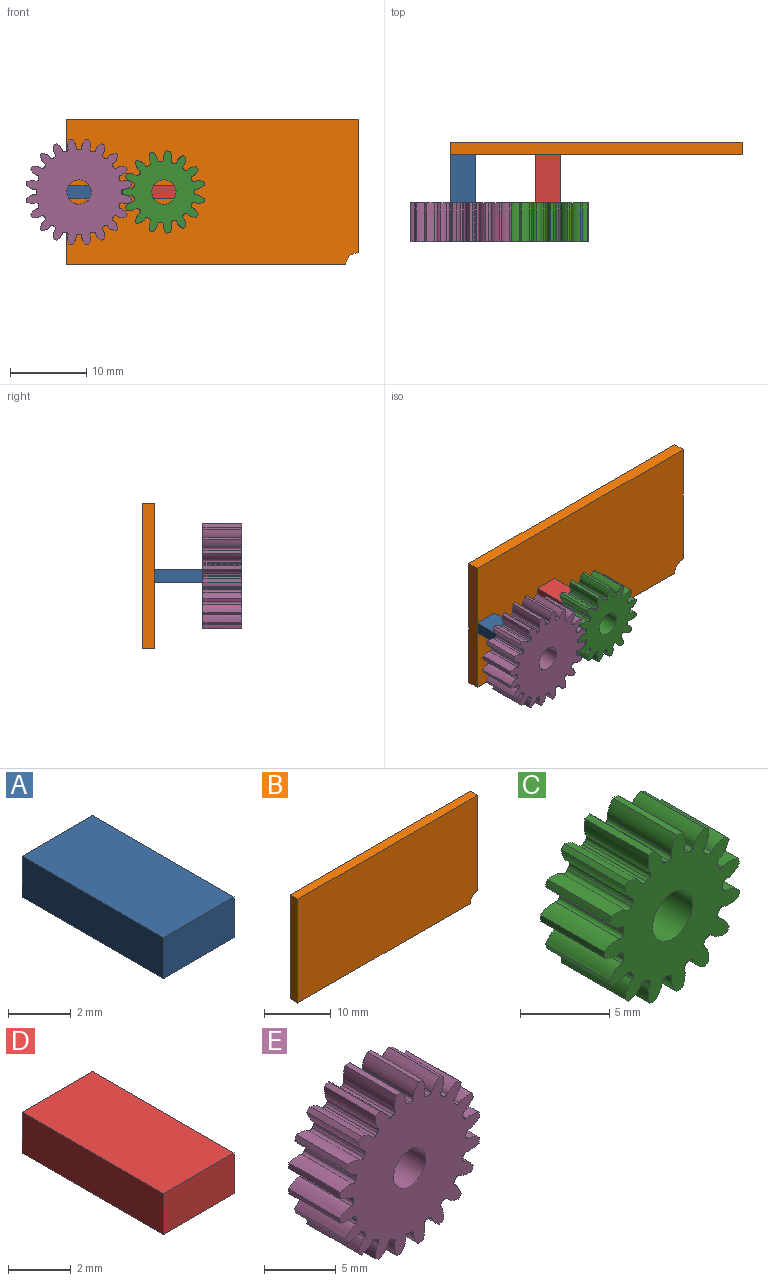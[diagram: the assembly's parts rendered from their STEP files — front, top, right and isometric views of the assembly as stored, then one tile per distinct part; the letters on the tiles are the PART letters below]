
ASSEMBLY  parts=5 mates=3
PART A: 6 faces, bbox 3.2x6.4x1.6 mm
  f0: plane 6.35x1.59mm, normal (-1,0,0), area 10.1mm2, adj f1,f3,f4,f5
  f1: plane 6.35x3.18mm, normal (0,0,-1), area 20.2mm2, adj f0,f2,f4,f5
  f2: plane 6.35x1.59mm, normal (1,0,0), area 10.1mm2, adj f1,f3,f4,f5
  f3: plane 6.35x3.18mm, normal (0,0,1), area 20.2mm2, adj f0,f2,f4,f5
  f4: plane 3.18x1.59mm, normal (0,-1,0), area 5mm2, adj f0,f1,f2,f3
  f5: plane 3.18x1.59mm, normal (0,1,0), area 5mm2, adj f0,f1,f2,f3
PART B: 7 faces, bbox 38.1x1.6x19.1 mm
  f0: plane 19.05x1.59mm, normal (-1,0,0), area 30.2mm2, adj f1,f3,f4,f5
  f1: plane 36.51x1.59mm, normal (0,0,-1), area 58mm2, adj f0,f4,f5,f6
  f2: plane 17.46x1.59mm, normal (1,0,0), area 27.7mm2, adj f3,f4,f5,f6
  f3: plane 38.1x1.59mm, normal (0,0,1), area 60.5mm2, adj f0,f2,f4,f5
  f4: plane 38.1x19.05mm, normal (0,-1,0), area 723.8mm2, adj f0,f1,f2,f3,f6
  f5: plane 38.1x19.05mm, normal (0,1,0), area 723.8mm2, adj f0,f1,f2,f3,f6
  f6: cylinder r=1.59mm len=1.59mm, axis (0,-1,0), area 4mm2, adj f1,f2,f4,f5
PART C: 93 faces, bbox 10.7x5.1x10.8 mm
  f0: cylinder r=5.4mm len=5.08mm, axis (0,1,0), area 2.1mm2, adj f14,f16,f82,f89
  f1: cylinder r=5.4mm len=5.08mm, axis (0,1,0), area 2.1mm2, adj f14,f16,f72,f84
  f2: cylinder r=5.4mm len=5.08mm, axis (0,1,0), area 2.1mm2, adj f14,f16,f17,f79
  f3: cylinder r=5.4mm len=5.08mm, axis (0,1,0), area 2.1mm2, adj f14,f16,f74,f77
  f4: cylinder r=5.4mm len=5.08mm, axis (0,1,0), area 2.1mm2, adj f14,f16,f62,f69
  f5: cylinder r=5.4mm len=5.08mm, axis (0,1,0), area 2.1mm2, adj f14,f16,f64,f87
  f6: cylinder r=5.4mm len=5.08mm, axis (0,1,0), area 2.1mm2, adj f14,f16,f59,f67
  f7: cylinder r=5.4mm len=5.08mm, axis (0,1,0), area 2.1mm2, adj f14,f16,f54,f57
  f8: cylinder r=5.4mm len=5.08mm, axis (0,1,0), area 2.1mm2, adj f14,f16,f37,f49
  f9: cylinder r=5.4mm len=5.08mm, axis (0,1,0), area 2.1mm2, adj f14,f16,f44,f47
  f10: cylinder r=5.4mm len=5.08mm, axis (0,1,0), area 2.1mm2, adj f14,f16,f32,f39
  f11: cylinder r=5.4mm len=5.08mm, axis (0,1,0), area 2.1mm2, adj f14,f16,f22,f34
  f12: cylinder r=5.4mm len=5.08mm, axis (0,1,0), area 2.1mm2, adj f14,f16,f29,f52
  f13: cylinder r=5.4mm len=5.08mm, axis (0,1,0), area 2.1mm2, adj f14,f16,f24,f27
  f14: plane 10.79x10.73mm, normal (0,-1,0), area 61.3mm2, adj f0,f1,f2,f3,f4,f5,f6,f7
  f15: cylinder r=5.4mm len=5.08mm, axis (0,1,0), area 2.1mm2, adj f14,f16,f19,f42
  f16: plane 10.79x10.73mm, normal (0,1,0), area 61.3mm2, adj f0,f1,f2,f3,f4,f5,f6,f7
  f17: extruded ~5.08x1.11mm, area 6.5mm2, adj f2,f14,f16,f20
  f18: cylinder r=3.97mm len=5.08mm, axis (0,1,0), area 1.1mm2, adj f14,f16,f20,f21
  f19: extruded ~5.08x1.11mm, area 6.5mm2, adj f14,f15,f16,f21
  f20: cylinder r=0.26mm len=5.08mm, axis (0,1,0), area 2mm2, adj f14,f16,f17,f18
  f21: cylinder r=0.26mm len=5.08mm, axis (0,1,0), area 2mm2, adj f14,f16,f18,f19
  f22: extruded ~5.08x1.24mm, area 6.5mm2, adj f11,f14,f16,f25
  f23: cylinder r=3.97mm len=5.08mm, axis (0,1,0), area 1.1mm2, adj f14,f16,f25,f26
  f24: extruded ~5.08x1.03mm, area 6.5mm2, adj f13,f14,f16,f26
  f25: cylinder r=0.26mm len=5.08mm, axis (0,1,0), area 2mm2, adj f14,f16,f22,f23
  f26: cylinder r=0.26mm len=5.08mm, axis (0,1,0), area 2mm2, adj f14,f16,f23,f24
  f27: extruded ~5.08x1.09mm, area 6.5mm2, adj f13,f14,f16,f30
  f28: cylinder r=3.97mm len=5.08mm, axis (0,1,0), area 1.1mm2, adj f14,f16,f30,f31
  f29: extruded ~5.08x1.22mm, area 6.5mm2, adj f12,f14,f16,f31
  f30: cylinder r=0.26mm len=5.08mm, axis (0,1,0), area 2mm2, adj f14,f16,f27,f28
  f31: cylinder r=0.26mm len=5.08mm, axis (0,1,0), area 2mm2, adj f14,f16,f28,f29
  f32: extruded ~5.08x1.17mm, area 6.5mm2, adj f10,f14,f16,f35
  f33: cylinder r=3.97mm len=5.08mm, axis (0,1,0), area 1.1mm2, adj f14,f16,f35,f36
  f34: extruded ~5.08x1.05mm, area 6.5mm2, adj f11,f14,f16,f36
  f35: cylinder r=0.26mm len=5.08mm, axis (0,1,0), area 2mm2, adj f14,f16,f32,f33
  f36: cylinder r=0.26mm len=5.08mm, axis (0,1,0), area 2mm2, adj f14,f16,f33,f34
  f37: extruded ~5.08x0.89mm, area 6.5mm2, adj f8,f14,f16,f40
  f38: cylinder r=3.97mm len=5.08mm, axis (0,1,0), area 1.1mm2, adj f14,f16,f40,f41
  f39: extruded ~5.08x1.23mm, area 6.5mm2, adj f10,f14,f16,f41
  f40: cylinder r=0.26mm len=5.08mm, axis (0,1,0), area 2mm2, adj f14,f16,f37,f38
  f41: cylinder r=0.26mm len=5.08mm, axis (0,1,0), area 2mm2, adj f14,f16,f38,f39
  f42: extruded ~5.08x1.24mm, area 6.5mm2, adj f14,f15,f16,f45
  f43: cylinder r=3.97mm len=5.08mm, axis (0,1,0), area 1.1mm2, adj f14,f16,f45,f46
  f44: extruded ~5.08x0.95mm, area 6.5mm2, adj f9,f14,f16,f46
  f45: cylinder r=0.26mm len=5.08mm, axis (0,1,0), area 2mm2, adj f14,f16,f42,f43
  f46: cylinder r=0.26mm len=5.08mm, axis (0,1,0), area 2mm2, adj f14,f16,f43,f44
  f47: extruded ~5.08x1.15mm, area 6.5mm2, adj f9,f14,f16,f50
  f48: cylinder r=3.97mm len=5.08mm, axis (0,1,0), area 1.1mm2, adj f14,f16,f50,f51
  f49: extruded ~5.08x1.19mm, area 6.5mm2, adj f8,f14,f16,f51
  f50: cylinder r=0.26mm len=5.08mm, axis (0,1,0), area 2mm2, adj f14,f16,f47,f48
  f51: cylinder r=0.26mm len=5.08mm, axis (0,1,0), area 2mm2, adj f14,f16,f48,f49
  f52: extruded ~5.08x0.98mm, area 6.5mm2, adj f12,f14,f16,f55
  f53: cylinder r=3.97mm len=5.08mm, axis (0,1,0), area 1.1mm2, adj f14,f16,f55,f56
  f54: extruded ~5.08x1.2mm, area 6.5mm2, adj f7,f14,f16,f56
  f55: cylinder r=0.26mm len=5.08mm, axis (0,1,0), area 2mm2, adj f14,f16,f52,f53
  f56: cylinder r=0.26mm len=5.08mm, axis (0,1,0), area 2mm2, adj f14,f16,f53,f54
  f57: extruded ~5.08x1.2mm, area 6.5mm2, adj f7,f14,f16,f60
  f58: cylinder r=3.97mm len=5.08mm, axis (0,1,0), area 1.1mm2, adj f14,f16,f60,f61
  f59: extruded ~5.08x0.98mm, area 6.5mm2, adj f6,f14,f16,f61
  f60: cylinder r=0.26mm len=5.08mm, axis (0,1,0), area 2mm2, adj f14,f16,f57,f58
  f61: cylinder r=0.26mm len=5.08mm, axis (0,1,0), area 2mm2, adj f14,f16,f58,f59
  f62: extruded ~5.08x1.03mm, area 6.5mm2, adj f4,f14,f16,f65
  f63: cylinder r=3.97mm len=5.08mm, axis (0,1,0), area 1.1mm2, adj f14,f16,f65,f66
  f64: extruded ~5.08x1.24mm, area 6.5mm2, adj f5,f14,f16,f66
  f65: cylinder r=0.26mm len=5.08mm, axis (0,1,0), area 2mm2, adj f14,f16,f62,f63
  f66: cylinder r=0.26mm len=5.08mm, axis (0,1,0), area 2mm2, adj f14,f16,f63,f64
  f67: extruded ~5.08x1.22mm, area 6.5mm2, adj f6,f14,f16,f70
  f68: cylinder r=3.97mm len=5.08mm, axis (0,1,0), area 1.1mm2, adj f14,f16,f70,f71
  f69: extruded ~5.08x1.09mm, area 6.5mm2, adj f4,f14,f16,f71
  f70: cylinder r=0.26mm len=5.08mm, axis (0,1,0), area 2mm2, adj f14,f16,f67,f68
  f71: cylinder r=0.26mm len=5.08mm, axis (0,1,0), area 2mm2, adj f14,f16,f68,f69
  f72: extruded ~5.08x1.19mm, area 6.5mm2, adj f1,f14,f16,f75
  f73: cylinder r=3.97mm len=5.08mm, axis (0,1,0), area 1.1mm2, adj f14,f16,f75,f76
  f74: extruded ~5.08x1.15mm, area 6.5mm2, adj f3,f14,f16,f76
  f75: cylinder r=0.26mm len=5.08mm, axis (0,1,0), area 2mm2, adj f14,f16,f72,f73
  f76: cylinder r=0.26mm len=5.08mm, axis (0,1,0), area 2mm2, adj f14,f16,f73,f74
  f77: extruded ~5.08x0.95mm, area 6.5mm2, adj f3,f14,f16,f80
  f78: cylinder r=3.97mm len=5.08mm, axis (0,1,0), area 1.1mm2, adj f14,f16,f80,f81
  f79: extruded ~5.08x1.24mm, area 6.5mm2, adj f2,f14,f16,f81
  f80: cylinder r=0.26mm len=5.08mm, axis (0,1,0), area 2mm2, adj f14,f16,f77,f78
  f81: cylinder r=0.26mm len=5.08mm, axis (0,1,0), area 2mm2, adj f14,f16,f78,f79
  f82: extruded ~5.08x1.23mm, area 6.5mm2, adj f0,f14,f16,f85
  f83: cylinder r=3.97mm len=5.08mm, axis (0,1,0), area 1.1mm2, adj f14,f16,f85,f86
  f84: extruded ~5.08x0.89mm, area 6.5mm2, adj f1,f14,f16,f86
  f85: cylinder r=0.26mm len=5.08mm, axis (0,1,0), area 2mm2, adj f14,f16,f82,f83
  f86: cylinder r=0.26mm len=5.08mm, axis (0,1,0), area 2mm2, adj f14,f16,f83,f84
  f87: extruded ~5.08x1.05mm, area 6.5mm2, adj f5,f14,f16,f90
  f88: cylinder r=3.97mm len=5.08mm, axis (0,1,0), area 1.1mm2, adj f14,f16,f90,f91
  f89: extruded ~5.08x1.17mm, area 6.5mm2, adj f0,f14,f16,f91
  f90: cylinder r=0.26mm len=5.08mm, axis (0,1,0), area 2mm2, adj f14,f16,f87,f88
  f91: cylinder r=0.26mm len=5.08mm, axis (0,1,0), area 2mm2, adj f14,f16,f88,f89
  f92: cylinder r=1.59mm len=5.08mm, axis (0,-1,0), area 50.7mm2, adj f14,f16
PART D: 6 faces, bbox 3.2x6.4x1.6 mm
  f0: plane 6.35x1.59mm, normal (-1,0,0), area 10.1mm2, adj f1,f3,f4,f5
  f1: plane 6.35x3.18mm, normal (0,0,-1), area 20.2mm2, adj f0,f2,f4,f5
  f2: plane 6.35x1.59mm, normal (1,0,0), area 10.1mm2, adj f1,f3,f4,f5
  f3: plane 6.35x3.18mm, normal (0,0,1), area 20.2mm2, adj f0,f2,f4,f5
  f4: plane 3.18x1.59mm, normal (0,-1,0), area 5mm2, adj f0,f1,f2,f3
  f5: plane 3.18x1.59mm, normal (0,1,0), area 5mm2, adj f0,f1,f2,f3
PART E: 123 faces, bbox 13.9x5.1x13.9 mm
  f0: cylinder r=6.99mm len=5.08mm, axis (0,1,0), area 2.2mm2, adj f19,f21,f72,f119
  f1: cylinder r=6.99mm len=5.08mm, axis (0,1,0), area 2.2mm2, adj f19,f21,f114,f117
  f2: cylinder r=6.99mm len=5.08mm, axis (0,1,0), area 2.2mm2, adj f19,f21,f109,f112
  f3: cylinder r=6.99mm len=5.08mm, axis (0,1,0), area 2.2mm2, adj f19,f21,f104,f107
  f4: cylinder r=6.99mm len=5.08mm, axis (0,1,0), area 2.2mm2, adj f19,f21,f99,f102
  f5: cylinder r=6.99mm len=5.08mm, axis (0,1,0), area 2.2mm2, adj f19,f21,f94,f97
  f6: cylinder r=6.99mm len=5.08mm, axis (0,1,0), area 2.2mm2, adj f19,f21,f89,f92
  f7: cylinder r=6.99mm len=5.08mm, axis (0,1,0), area 2.2mm2, adj f19,f21,f84,f87
  f8: cylinder r=6.99mm len=5.08mm, axis (0,1,0), area 2.2mm2, adj f19,f21,f67,f79
  f9: cylinder r=6.99mm len=5.08mm, axis (0,1,0), area 2.2mm2, adj f19,f21,f74,f77
  f10: cylinder r=6.99mm len=5.08mm, axis (0,1,0), area 2.2mm2, adj f19,f21,f62,f69
  f11: cylinder r=6.99mm len=5.08mm, axis (0,1,0), area 2.2mm2, adj f19,f21,f42,f64
  f12: cylinder r=6.99mm len=5.08mm, axis (0,1,0), area 2.2mm2, adj f19,f21,f22,f59
  f13: cylinder r=6.99mm len=5.08mm, axis (0,1,0), area 2.2mm2, adj f19,f21,f54,f57
  f14: cylinder r=6.99mm len=5.08mm, axis (0,1,0), area 2.2mm2, adj f19,f21,f49,f52
  f15: cylinder r=6.99mm len=5.08mm, axis (0,1,0), area 2.2mm2, adj f19,f21,f44,f47
  f16: cylinder r=6.99mm len=5.08mm, axis (0,1,0), area 2.2mm2, adj f19,f21,f32,f39
  f17: cylinder r=6.99mm len=5.08mm, axis (0,1,0), area 2.2mm2, adj f19,f21,f34,f82
  f18: cylinder r=6.99mm len=5.08mm, axis (0,1,0), area 2.2mm2, adj f19,f21,f29,f37
  f19: plane 13.87x13.87mm, normal (0,-1,0), area 116.2mm2, adj f0,f1,f2,f3,f4,f5,f6,f7
  f20: cylinder r=6.99mm len=5.08mm, axis (0,1,0), area 2.2mm2, adj f19,f21,f24,f27
  f21: plane 13.87x13.87mm, normal (0,1,0), area 116.2mm2, adj f0,f1,f2,f3,f4,f5,f6,f7
  f22: extruded ~5.08x1.14mm, area 6.5mm2, adj f12,f19,f21,f25
  f23: cylinder r=5.56mm len=5.08mm, axis (0,1,0), area 1.1mm2, adj f19,f21,f25,f26
  f24: extruded ~5.08x1.14mm, area 6.5mm2, adj f19,f20,f21,f26
  f25: cylinder r=0.25mm len=5.08mm, axis (0,1,0), area 2mm2, adj f19,f21,f22,f23
  f26: cylinder r=0.25mm len=5.08mm, axis (0,1,0), area 2mm2, adj f19,f21,f23,f24
  f27: extruded ~5.08x1.24mm, area 6.5mm2, adj f19,f20,f21,f30
  f28: cylinder r=5.56mm len=5.08mm, axis (0,1,0), area 1.1mm2, adj f19,f21,f30,f31
  f29: extruded ~5.08x0.93mm, area 6.5mm2, adj f18,f19,f21,f31
  f30: cylinder r=0.25mm len=5.08mm, axis (0,1,0), area 2mm2, adj f19,f21,f27,f28
  f31: cylinder r=0.25mm len=5.08mm, axis (0,1,0), area 2mm2, adj f19,f21,f28,f29
  f32: extruded ~5.08x1.08mm, area 6.5mm2, adj f16,f19,f21,f35
  f33: cylinder r=5.56mm len=5.08mm, axis (0,1,0), area 1.1mm2, adj f19,f21,f35,f36
  f34: extruded ~5.08x1.22mm, area 6.5mm2, adj f17,f19,f21,f36
  f35: cylinder r=0.25mm len=5.08mm, axis (0,1,0), area 2mm2, adj f19,f21,f32,f33
  f36: cylinder r=0.25mm len=5.08mm, axis (0,1,0), area 2mm2, adj f19,f21,f33,f34
  f37: extruded ~5.08x1.22mm, area 6.5mm2, adj f18,f19,f21,f40
  f38: cylinder r=5.56mm len=5.08mm, axis (0,1,0), area 1.1mm2, adj f19,f21,f40,f41
  f39: extruded ~5.08x1.08mm, area 6.5mm2, adj f16,f19,f21,f41
  f40: cylinder r=0.25mm len=5.08mm, axis (0,1,0), area 2mm2, adj f19,f21,f37,f38
  f41: cylinder r=0.25mm len=5.08mm, axis (0,1,0), area 2mm2, adj f19,f21,f38,f39
  f42: extruded ~5.08x1.24mm, area 6.5mm2, adj f11,f19,f21,f45
  f43: cylinder r=5.56mm len=5.08mm, axis (0,1,0), area 1.1mm2, adj f19,f21,f45,f46
  f44: extruded ~5.08x0.93mm, area 6.5mm2, adj f15,f19,f21,f46
  f45: cylinder r=0.25mm len=5.08mm, axis (0,1,0), area 2mm2, adj f19,f21,f42,f43
  f46: cylinder r=0.25mm len=5.08mm, axis (0,1,0), area 2mm2, adj f19,f21,f43,f44
  f47: extruded ~5.08x1.22mm, area 6.5mm2, adj f15,f19,f21,f50
  f48: cylinder r=5.56mm len=5.08mm, axis (0,1,0), area 1.1mm2, adj f19,f21,f50,f51
  f49: extruded ~5.08x1.08mm, area 6.5mm2, adj f14,f19,f21,f51
  f50: cylinder r=0.25mm len=5.08mm, axis (0,1,0), area 2mm2, adj f19,f21,f47,f48
  f51: cylinder r=0.25mm len=5.08mm, axis (0,1,0), area 2mm2, adj f19,f21,f48,f49
  f52: extruded ~5.08x1.08mm, area 6.5mm2, adj f14,f19,f21,f55
  f53: cylinder r=5.56mm len=5.08mm, axis (0,1,0), area 1.1mm2, adj f19,f21,f55,f56
  f54: extruded ~5.08x1.22mm, area 6.5mm2, adj f13,f19,f21,f56
  f55: cylinder r=0.25mm len=5.08mm, axis (0,1,0), area 2mm2, adj f19,f21,f52,f53
  f56: cylinder r=0.25mm len=5.08mm, axis (0,1,0), area 2mm2, adj f19,f21,f53,f54
  f57: extruded ~5.08x0.93mm, area 6.5mm2, adj f13,f19,f21,f60
  f58: cylinder r=5.56mm len=5.08mm, axis (0,1,0), area 1.1mm2, adj f19,f21,f60,f61
  f59: extruded ~5.08x1.24mm, area 6.5mm2, adj f12,f19,f21,f61
  f60: cylinder r=0.25mm len=5.08mm, axis (0,1,0), area 2mm2, adj f19,f21,f57,f58
  f61: cylinder r=0.25mm len=5.08mm, axis (0,1,0), area 2mm2, adj f19,f21,f58,f59
  f62: extruded ~5.08x1.14mm, area 6.5mm2, adj f10,f19,f21,f65
  f63: cylinder r=5.56mm len=5.08mm, axis (0,1,0), area 1.1mm2, adj f19,f21,f65,f66
  f64: extruded ~5.08x1.14mm, area 6.5mm2, adj f11,f19,f21,f66
  f65: cylinder r=0.25mm len=5.08mm, axis (0,1,0), area 2mm2, adj f19,f21,f62,f63
  f66: cylinder r=0.25mm len=5.08mm, axis (0,1,0), area 2mm2, adj f19,f21,f63,f64
  f67: extruded ~5.08x0.93mm, area 6.5mm2, adj f8,f19,f21,f70
  f68: cylinder r=5.56mm len=5.08mm, axis (0,1,0), area 1.1mm2, adj f19,f21,f70,f71
  f69: extruded ~5.08x1.24mm, area 6.5mm2, adj f10,f19,f21,f71
  f70: cylinder r=0.25mm len=5.08mm, axis (0,1,0), area 2mm2, adj f19,f21,f67,f68
  f71: cylinder r=0.25mm len=5.08mm, axis (0,1,0), area 2mm2, adj f19,f21,f68,f69
  f72: extruded ~5.08x1.22mm, area 6.5mm2, adj f0,f19,f21,f75
  f73: cylinder r=5.56mm len=5.08mm, axis (0,1,0), area 1.1mm2, adj f19,f21,f75,f76
  f74: extruded ~5.08x1.08mm, area 6.5mm2, adj f9,f19,f21,f76
  f75: cylinder r=0.25mm len=5.08mm, axis (0,1,0), area 2mm2, adj f19,f21,f72,f73
  f76: cylinder r=0.25mm len=5.08mm, axis (0,1,0), area 2mm2, adj f19,f21,f73,f74
  f77: extruded ~5.08x1.08mm, area 6.5mm2, adj f9,f19,f21,f80
  f78: cylinder r=5.56mm len=5.08mm, axis (0,1,0), area 1.1mm2, adj f19,f21,f80,f81
  f79: extruded ~5.08x1.22mm, area 6.5mm2, adj f8,f19,f21,f81
  f80: cylinder r=0.25mm len=5.08mm, axis (0,1,0), area 2mm2, adj f19,f21,f77,f78
  f81: cylinder r=0.25mm len=5.08mm, axis (0,1,0), area 2mm2, adj f19,f21,f78,f79
  f82: extruded ~5.08x0.93mm, area 6.5mm2, adj f17,f19,f21,f85
  f83: cylinder r=5.56mm len=5.08mm, axis (0,1,0), area 1.1mm2, adj f19,f21,f85,f86
  f84: extruded ~5.08x1.24mm, area 6.5mm2, adj f7,f19,f21,f86
  f85: cylinder r=0.25mm len=5.08mm, axis (0,1,0), area 2mm2, adj f19,f21,f82,f83
  f86: cylinder r=0.25mm len=5.08mm, axis (0,1,0), area 2mm2, adj f19,f21,f83,f84
  f87: extruded ~5.08x1.14mm, area 6.5mm2, adj f7,f19,f21,f90
  f88: cylinder r=5.56mm len=5.08mm, axis (0,1,0), area 1.1mm2, adj f19,f21,f90,f91
  f89: extruded ~5.08x1.14mm, area 6.5mm2, adj f6,f19,f21,f91
  f90: cylinder r=0.25mm len=5.08mm, axis (0,1,0), area 2mm2, adj f19,f21,f87,f88
  f91: cylinder r=0.25mm len=5.08mm, axis (0,1,0), area 2mm2, adj f19,f21,f88,f89
  f92: extruded ~5.08x1.24mm, area 6.5mm2, adj f6,f19,f21,f95
  f93: cylinder r=5.56mm len=5.08mm, axis (0,1,0), area 1.1mm2, adj f19,f21,f95,f96
  f94: extruded ~5.08x0.93mm, area 6.5mm2, adj f5,f19,f21,f96
  f95: cylinder r=0.25mm len=5.08mm, axis (0,1,0), area 2mm2, adj f19,f21,f92,f93
  f96: cylinder r=0.25mm len=5.08mm, axis (0,1,0), area 2mm2, adj f19,f21,f93,f94
  f97: extruded ~5.08x1.22mm, area 6.5mm2, adj f5,f19,f21,f100
  f98: cylinder r=5.56mm len=5.08mm, axis (0,1,0), area 1.1mm2, adj f19,f21,f100,f101
  f99: extruded ~5.08x1.08mm, area 6.5mm2, adj f4,f19,f21,f101
  f100: cylinder r=0.25mm len=5.08mm, axis (0,1,0), area 2mm2, adj f19,f21,f97,f98
  f101: cylinder r=0.25mm len=5.08mm, axis (0,1,0), area 2mm2, adj f19,f21,f98,f99
  f102: extruded ~5.08x1.08mm, area 6.5mm2, adj f4,f19,f21,f105
  f103: cylinder r=5.56mm len=5.08mm, axis (0,1,0), area 1.1mm2, adj f19,f21,f105,f106
  f104: extruded ~5.08x1.22mm, area 6.5mm2, adj f3,f19,f21,f106
  f105: cylinder r=0.25mm len=5.08mm, axis (0,1,0), area 2mm2, adj f19,f21,f102,f103
  f106: cylinder r=0.25mm len=5.08mm, axis (0,1,0), area 2mm2, adj f19,f21,f103,f104
  f107: extruded ~5.08x0.93mm, area 6.5mm2, adj f3,f19,f21,f110
  f108: cylinder r=5.56mm len=5.08mm, axis (0,1,0), area 1.1mm2, adj f19,f21,f110,f111
  f109: extruded ~5.08x1.24mm, area 6.5mm2, adj f2,f19,f21,f111
  f110: cylinder r=0.25mm len=5.08mm, axis (0,1,0), area 2mm2, adj f19,f21,f107,f108
  f111: cylinder r=0.25mm len=5.08mm, axis (0,1,0), area 2mm2, adj f19,f21,f108,f109
  f112: extruded ~5.08x1.14mm, area 6.5mm2, adj f2,f19,f21,f115
  f113: cylinder r=5.56mm len=5.08mm, axis (0,1,0), area 1.1mm2, adj f19,f21,f115,f116
  f114: extruded ~5.08x1.14mm, area 6.5mm2, adj f1,f19,f21,f116
  f115: cylinder r=0.25mm len=5.08mm, axis (0,1,0), area 2mm2, adj f19,f21,f112,f113
  f116: cylinder r=0.25mm len=5.08mm, axis (0,1,0), area 2mm2, adj f19,f21,f113,f114
  f117: extruded ~5.08x1.24mm, area 6.5mm2, adj f1,f19,f21,f120
  f118: cylinder r=5.56mm len=5.08mm, axis (0,1,0), area 1.1mm2, adj f19,f21,f120,f121
  f119: extruded ~5.08x0.93mm, area 6.5mm2, adj f0,f19,f21,f121
  f120: cylinder r=0.25mm len=5.08mm, axis (0,1,0), area 2mm2, adj f19,f21,f117,f118
  f121: cylinder r=0.25mm len=5.08mm, axis (0,1,0), area 2mm2, adj f19,f21,f118,f119
  f122: cylinder r=1.59mm len=5.08mm, axis (0,-1,0), area 50.7mm2, adj f19,f21
PLACE A t=(1.55,-1.6,0.56)mm
PLACE B t=(7.9,-0.01,0.56)mm
PLACE C t=(-17.5,-7.95,10.08)mm
PLACE D t=(1.55,-1.6,0.56)mm
PLACE E t=(-28.62,-7.95,10.08)mm
MATE fastened C.f0 <-> D.f4  axis (0,1,0) through (-17.5,-7.95,10.08)mm
MATE fastened E.f0 <-> A.f4  axis (0,1,0) through (-28.62,-7.95,10.08)mm
MATE fastened B.f4 <-> A.f5  axis (0,-1,0) through (-30.2,-1.6,10.08)mm
